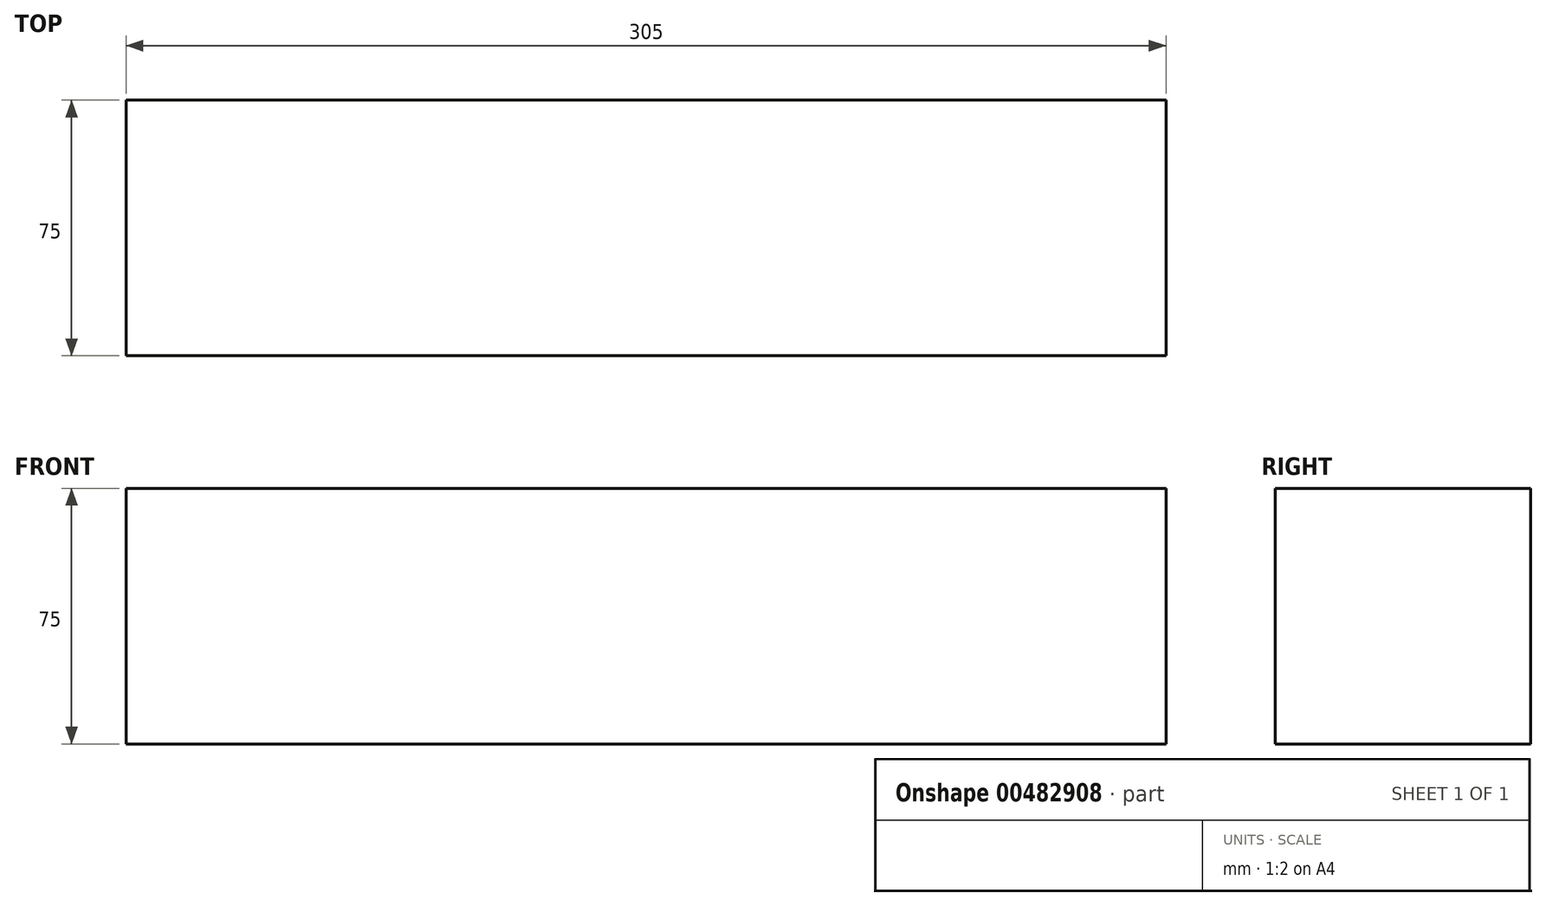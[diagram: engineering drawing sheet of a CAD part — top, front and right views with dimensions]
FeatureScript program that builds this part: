
annotation { "Feature Type Name" : "Feature", "Feature Type Description" : "" }
export const myFeature = defineFeature(function(context is Context, id is Id, definition is map)
    precondition{}
    {
        {
            var Q0;
            Q0=qCreatedBy(makeId("Top.planeOp"),FACE);
            var sketch = newSketch(context, id + "F0", { "sketchPlane" : qUnion([Q0])});
            skLineSegment(sketch, "E0.bottom", {"start": v(-152.5, 37.5) * mm, "end": v(152.5, 37.5) * mm});
            skLineSegment(sketch, "E0.top", {"start": v(-152.5, -37.5) * mm, "end": v(152.5, -37.5) * mm});
            skLineSegment(sketch, "E0.left", {"start": v(-152.5, 37.5) * mm, "end": v(-152.5, -37.5) * mm});
            skLineSegment(sketch, "E0.right", {"start": v(152.5, 37.5) * mm, "end": v(152.5, -37.5) * mm});
            skPoint(sketch, "E0.middle", {"position": v(0, 0) * mm});
            skSolve(sketch);
        }
        {
            var Q0;
            Q0=makeQuery(id+"F0.imprint","IMPRINT",FACE,{"disambiguationData":[TD([[makeQuery(id+"F0.imprint","IMPRINT",EDGE,{"derivedFrom":sQuery(id+"F0.wireOp",EDGE,"E0.bottom")}),-1.0]])]});
            extrude(context, id + "F1", {"entities" : qUnion([Q0]), "depth" : 75 * mm});
        }
        {
            var Q0;
            Q0=makeQuery(id+"F1.opExtrude","SWEPT_FACE",FACE,{"disambiguationData":[OSD([sQuery(id+"F0.wireOp",EDGE,"E0.left")])]});
            var sketch = newSketch(context, id + "F2", { "sketchPlane" : qUnion([Q0])});
            skCircle(sketch, "E1", {"center": v(-0.5, 43) * mm, "radius": 9.5 * mm});
            skSolve(sketch);
        }
        {
            var Q0;
            Q0=makeQuery(id+"F2.imprint","IMPRINT",FACE,{"disambiguationData":[TD([[makeQuery(id+"F2.imprint","IMPRINT",EDGE,{"derivedFrom":sQuery(id+"F2.wireOp",EDGE,"E1")}),1.0]])]});
            extrude(context, id + "F3", {"entities" : qUnion([Q0]), "operationType" : NewBodyOperationType.ADD, "oppositeDirection" : true, "depth" : 55 * mm});
        }
    });
